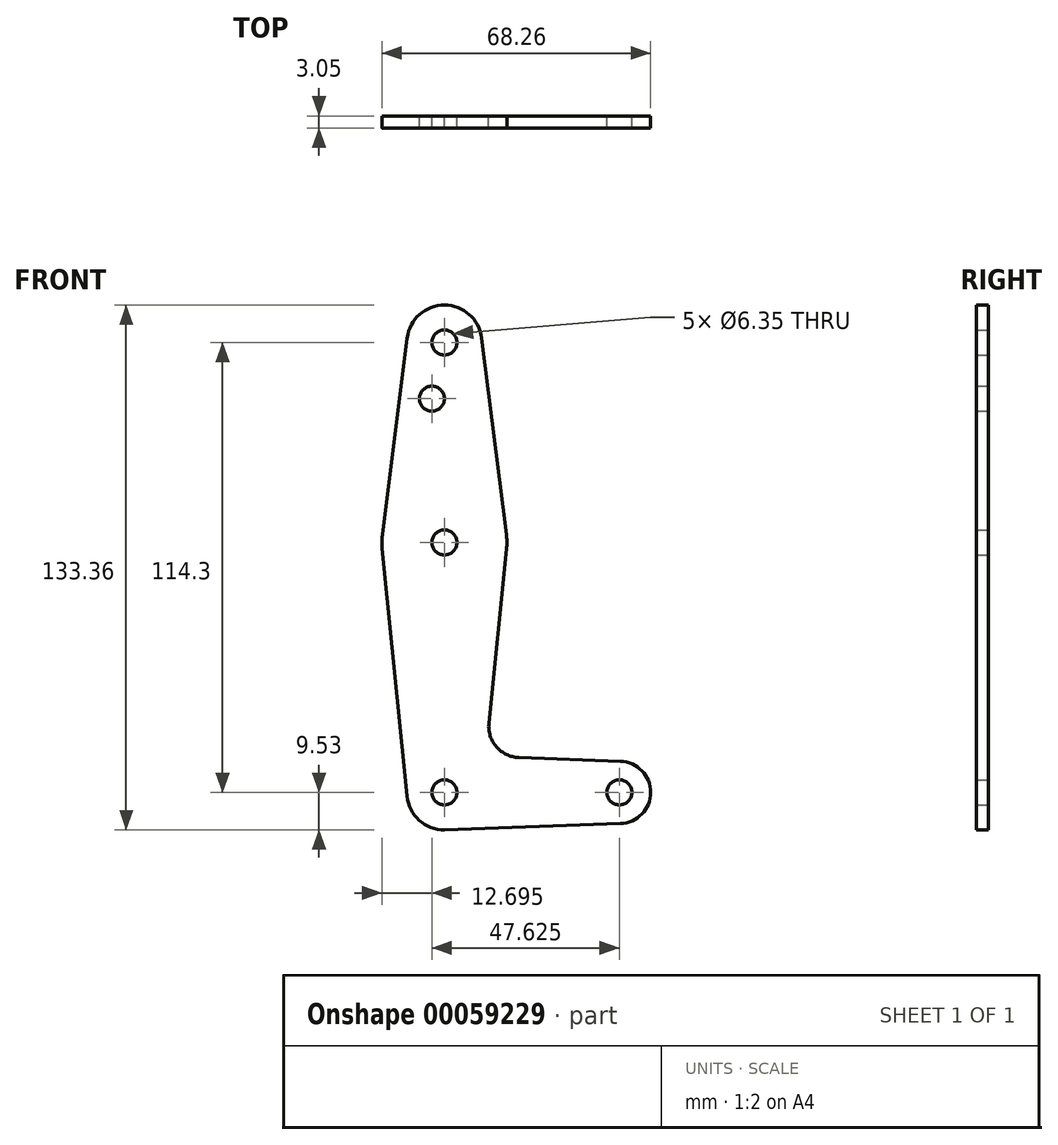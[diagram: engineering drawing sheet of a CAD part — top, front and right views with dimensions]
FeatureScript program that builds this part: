
annotation { "Feature Type Name" : "Feature", "Feature Type Description" : "" }
export const myFeature = defineFeature(function(context is Context, id is Id, definition is map)
    precondition{}
    {
        {
            var Q0;
            Q0=qCreatedBy(makeId("Front.planeOp"),FACE);
            var sketch = newSketch(context, id + "F0", { "sketchPlane" : qUnion([Q0])});
            skLineSegment(sketch, "E0", {"start": v(0, 0) * mm, "end": v(44.45, 0) * mm});
            skLineSegment(sketch, "E1", {"start": v(0, 0) * mm, "end": v(0, 63.5) * mm});
            skLineSegment(sketch, "E2", {"start": v(0, 63.5) * mm, "end": v(0, 114.3) * mm});
            skCircle(sketch, "E3", {"center": v(0, 0) * mm, "radius": 3.18 * mm});
            skCircle(sketch, "E4", {"center": v(44.45, 0) * mm, "radius": 3.18 * mm});
            skCircle(sketch, "E5", {"center": v(0, 63.5) * mm, "radius": 3.18 * mm});
            skCircle(sketch, "E6", {"center": v(0, 114.3) * mm, "radius": 3.18 * mm});
            skLineSegment(sketch, "E7", {"start": v(0, 63.5) * mm, "end": v(0, 100.03) * mm});
            skLineSegment(sketch, "E8", {"start": v(0, 100.03) * mm, "end": v(-3.18, 100.03) * mm});
            skCircle(sketch, "E9", {"center": v(-3.18, 100.03) * mm, "radius": 3.18 * mm});
            skCircle(sketch, "E10", {"center": v(0, 114.3) * mm, "radius": 9.53 * mm});
            skCircle(sketch, "E11", {"center": v(0, 63.5) * mm, "radius": 15.88 * mm});
            skCircle(sketch, "E12", {"center": v(0, 0) * mm, "radius": 9.53 * mm});
            skCircle(sketch, "E13", {"center": v(44.45, 0) * mm, "radius": 7.94 * mm});
            skLineSegment(sketch, "E14", {"start": v(9.45, 115.5) * mm, "end": v(16, 63.57) * mm});
            skLineSegment(sketch, "E15", {"start": v(-9.45, 115.5) * mm, "end": v(-15.75, 65.48) * mm});
            skLineSegment(sketch, "E16", {"start": v(11.3, 17.6) * mm, "end": v(15.8, 61.9) * mm});
            skLineSegment(sketch, "E17", {"start": v(44.73, 7.93) * mm, "end": v(18.93, 8.85) * mm});
            skLineSegment(sketch, "E18", {"start": v(0, -9.53) * mm, "end": v(44.73, -7.93) * mm});
            skLineSegment(sketch, "E19", {"start": v(-9.48, -0.95) * mm, "end": v(-15.8, 61.91) * mm});
            skArc(sketch, "E20.filletArc", {"start": v(11.3, 17.6) * mm, "mid": v(12.58, 12.42) * mm, "end": v(16.85, 9.21) * mm});
            skPoint(sketch, "E21.visualSharp", {"position": v(18.93, 8.85) * mm});
            skArc(sketch, "E21.filletArc", {"start": v(16.85, 9.21) * mm, "mid": v(17.88, 8.96) * mm, "end": v(18.93, 8.85) * mm});
            skSolve(sketch);
        }
        {
            var Q0;
            {var subQ4=sQuery(id+"F0.wireOp",EDGE,"E9");Q0=makeQuery(id+"F0.imprint","IMPRINT",FACE,{"disambiguationData":[TD([[makeQuery(id+"F0.imprint","IMPRINT",EDGE,{"derivedFrom":subQ4}),-1.0]])]});}
            var Q1;
            {var subQ0=sQuery(id+"F0.wireOp",EDGE,"E14");var subQ5=sQuery(id+"F0.wireOp",EDGE,"E10");var subQ6=makeQuery(id+"F0.imprint","INTERSECT",VERTEX,{"derivedFrom":[subQ5,subQ0]});Q1=makeQuery(id+"F0.imprint","IMPRINT",FACE,{"disambiguationData":[TD([[makeQuery(id+"F0.imprint","IMPRINT",EDGE,{"disambiguationData":[TD([[subQ6,1.0]])],"derivedFrom":subQ5}),-1.0]])]});}
            var Q2;
            Q2=makeQuery(id+"F0.imprint","IMPRINT",FACE,{"disambiguationData":[TD([[makeQuery(id+"F0.imprint","IMPRINT",EDGE,{"derivedFrom":sQuery(id+"F0.wireOp",EDGE,"E6")}),-1.0]])]});
            var Q3;
            {var subQ3=sQuery(id+"F0.wireOp",EDGE,"E11");var subQ5=sQuery(id+"F0.wireOp",EDGE,"E1");var subQ7=makeQuery(id+"F0.imprint","INTERSECT",VERTEX,{"derivedFrom":[subQ5,subQ3]});Q3=makeQuery(id+"F0.imprint","IMPRINT",FACE,{"disambiguationData":[TD([[makeQuery(id+"F0.imprint","IMPRINT",EDGE,{"disambiguationData":[TD([[subQ7,-1.0]])],"derivedFrom":subQ5}),-1.0]])]});}
            var Q4;
            {var subQ0=sQuery(id+"F0.wireOp",EDGE,"E11");var subQ6=sQuery(id+"F0.wireOp",EDGE,"E1");var subQ8=makeQuery(id+"F0.imprint","INTERSECT",VERTEX,{"derivedFrom":[subQ6,subQ0]});Q4=makeQuery(id+"F0.imprint","IMPRINT",FACE,{"disambiguationData":[TD([[makeQuery(id+"F0.imprint","IMPRINT",EDGE,{"disambiguationData":[TD([[subQ8,-1.0]])],"derivedFrom":subQ6}),1.0]])]});}
            var Q5;
            {var subQ5=sQuery(id+"F0.wireOp",EDGE,"E16");Q5=makeQuery(id+"F0.imprint","IMPRINT",FACE,{"disambiguationData":[TD([[makeQuery(id+"F0.imprint","IMPRINT",EDGE,{"derivedFrom":subQ5}),1.0]])]});}
            var Q6;
            {var subQ0=sQuery(id+"F0.wireOp",EDGE,"E3");var subQ1=sQuery(id+"F0.wireOp",EDGE,"E0");var subQ2=makeQuery(id+"F0.imprint","INTERSECT",VERTEX,{"derivedFrom":[subQ1,subQ0]});Q6=makeQuery(id+"F0.imprint","IMPRINT",FACE,{"disambiguationData":[TD([[makeQuery(id+"F0.imprint","IMPRINT",EDGE,{"disambiguationData":[TD([[subQ2,-1.0]])],"derivedFrom":subQ1}),1.0]])]});}
            var Q7;
            {var subQ5=sQuery(id+"F0.wireOp",EDGE,"E19");Q7=makeQuery(id+"F0.imprint","IMPRINT",FACE,{"disambiguationData":[TD([[makeQuery(id+"F0.imprint","IMPRINT",EDGE,{"derivedFrom":subQ5}),-1.0]])]});}
            var Q8;
            {var subQ7=sQuery(id+"F0.wireOp",EDGE,"E3");var subQ8=sQuery(id+"F0.wireOp",EDGE,"E0");var subQ9=makeQuery(id+"F0.imprint","INTERSECT",VERTEX,{"derivedFrom":[subQ8,subQ7]});Q8=makeQuery(id+"F0.imprint","IMPRINT",FACE,{"disambiguationData":[TD([[makeQuery(id+"F0.imprint","IMPRINT",EDGE,{"disambiguationData":[TD([[subQ9,-1.0]])],"derivedFrom":subQ8}),-1.0]])]});}
            var Q9;
            {var subQ0=sQuery(id+"F0.wireOp",EDGE,"E13");var subQ1=sQuery(id+"F0.wireOp",EDGE,"E0");var subQ2=makeQuery(id+"F0.imprint","INTERSECT",VERTEX,{"derivedFrom":[subQ1,subQ0]});Q9=makeQuery(id+"F0.imprint","IMPRINT",FACE,{"disambiguationData":[TD([[makeQuery(id+"F0.imprint","IMPRINT",EDGE,{"disambiguationData":[TD([[subQ2,1.0]])],"derivedFrom":subQ1}),-1.0]])]});}
            var Q10;
            Q10=makeQuery(id+"F0.imprint","IMPRINT",FACE,{"disambiguationData":[TD([[makeQuery(id+"F0.imprint","IMPRINT",EDGE,{"derivedFrom":sQuery(id+"F0.wireOp",EDGE,"E4")}),-1.0]])]});
            extrude(context, id + "F1", {"entities" : qUnion([Q0, Q1, Q2, Q3, Q4, Q5, Q6, Q7, Q8, Q9, Q10]), "depth" : 3.05 * mm});
        }
    });
